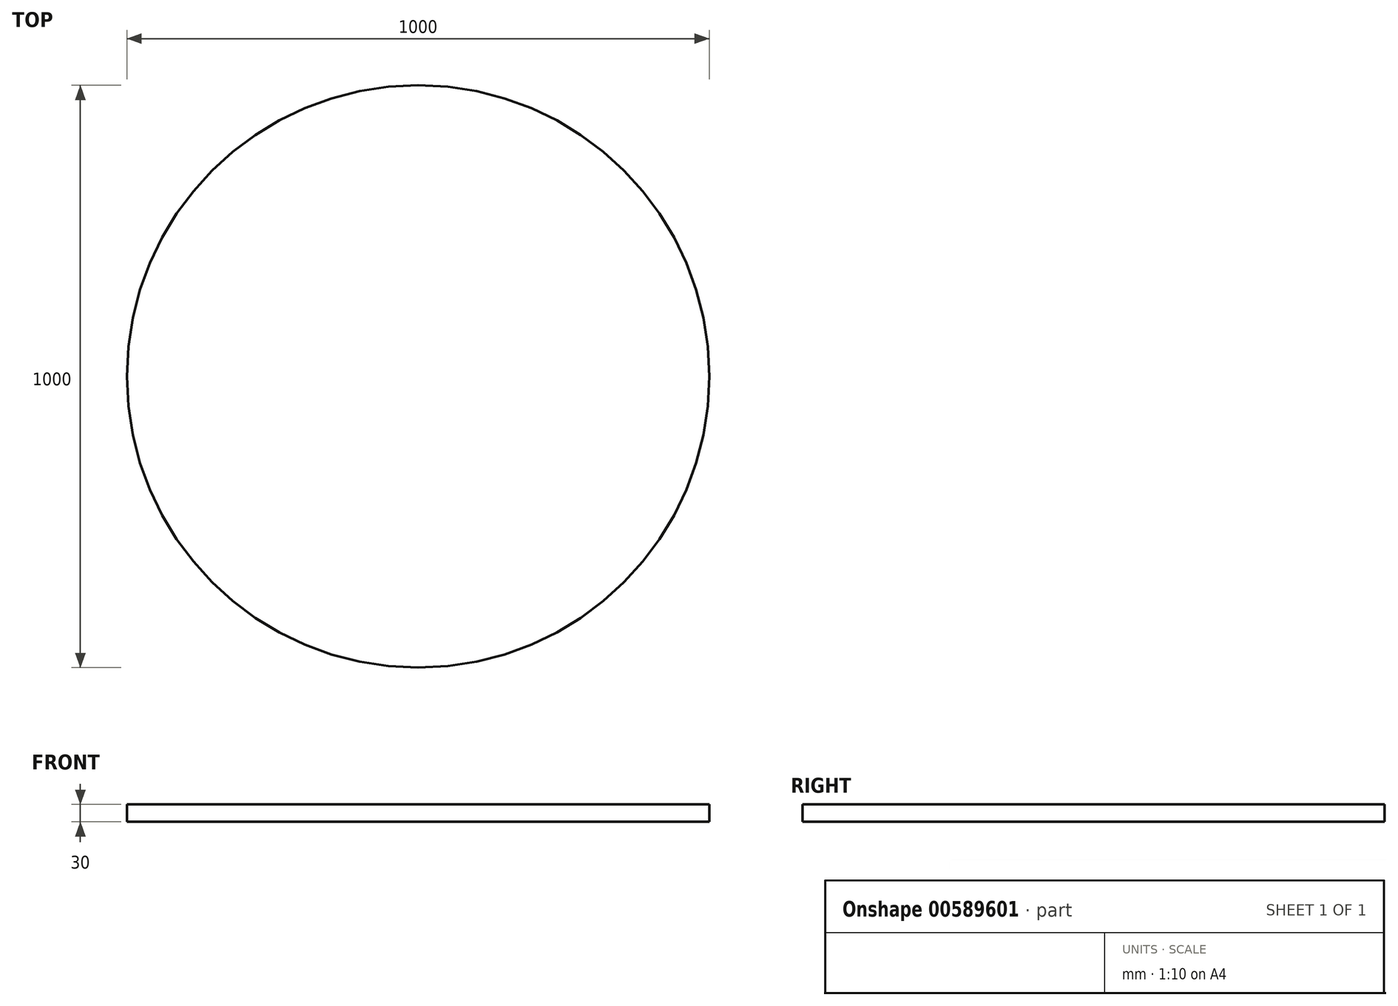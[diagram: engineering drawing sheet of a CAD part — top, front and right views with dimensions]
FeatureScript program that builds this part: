
annotation { "Feature Type Name" : "Feature", "Feature Type Description" : "" }
export const myFeature = defineFeature(function(context is Context, id is Id, definition is map)
    precondition{}
    {
        {
            var Q0;
            Q0=qCreatedBy(makeId("Top.planeOp"),FACE);
            var sketch = newSketch(context, id + "F0", { "sketchPlane" : qUnion([Q0])});
            skCircle(sketch, "E0", {"center": v(-46.92, 21.17) * mm, "radius": 500 * mm});
            skSolve(sketch);
        }
        {
            var Q0;
            Q0=makeQuery(id+"F0.imprint","IMPRINT",FACE,{"disambiguationData":[TD([[makeQuery(id+"F0.imprint","IMPRINT",EDGE,{"derivedFrom":sQuery(id+"F0.wireOp",EDGE,"E0")}),1.0]])]});
            extrude(context, id + "F1", {"entities" : qUnion([Q0]), "depth" : 30 * mm, "offsetDistance" : 25 * mm});
        }
    });
